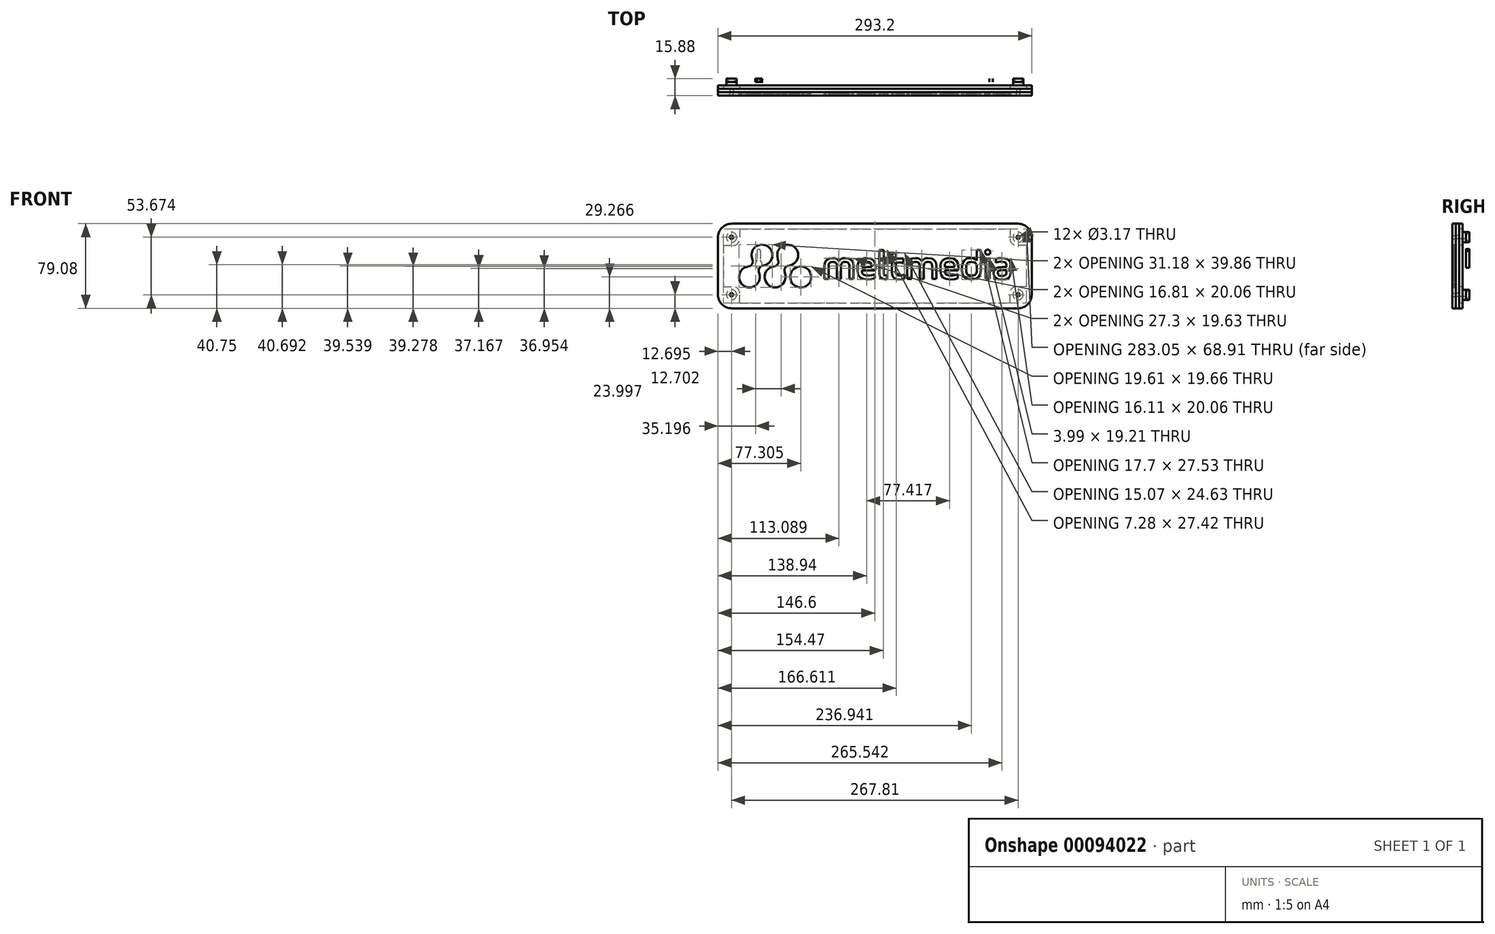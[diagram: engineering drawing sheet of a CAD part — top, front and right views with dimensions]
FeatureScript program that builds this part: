
annotation { "Feature Type Name" : "Feature", "Feature Type Description" : "" }
export const myFeature = defineFeature(function(context is Context, id is Id, definition is map)
    precondition{}
    {
        {
            var Q0;
            Q0=qCreatedBy(makeId("Front.planeOp"),FACE);
            var sketch = newSketch(context, id + "F0", { "sketchPlane" : qUnion([Q0])});
            skLineSegment(sketch, "E0", {"start": v(-43.17, -12.1) * mm, "end": v(-47.16, -12.1) * mm});
            skLineSegment(sketch, "E1", {"start": v(-47.16, -12.1) * mm, "end": v(-47.16, 0.02) * mm});
            skLineSegment(sketch, "E2", {"start": v(-47.16, 0.02) * mm, "end": v(-46.7, 3.2) * mm});
            skLineSegment(sketch, "E3", {"start": v(-46.7, 3.2) * mm, "end": v(-45.25, 5.57) * mm});
            skLineSegment(sketch, "E4", {"start": v(-45.25, 5.57) * mm, "end": v(-42.8, 7.03) * mm});
            skLineSegment(sketch, "E5", {"start": v(-42.8, 7.03) * mm, "end": v(-39.3, 7.53) * mm});
            skLineSegment(sketch, "E6", {"start": v(-39.3, 7.53) * mm, "end": v(-37.27, 7.34) * mm});
            skLineSegment(sketch, "E7", {"start": v(-37.27, 7.34) * mm, "end": v(-35.64, 6.79) * mm});
            skLineSegment(sketch, "E8", {"start": v(-35.64, 6.79) * mm, "end": v(-34.39, 5.9) * mm});
            skLineSegment(sketch, "E9", {"start": v(-34.39, 5.9) * mm, "end": v(-33.5, 4.7) * mm});
            skLineSegment(sketch, "E10", {"start": v(-33.5, 4.7) * mm, "end": v(-32.57, 5.9) * mm});
            skLineSegment(sketch, "E11", {"start": v(-32.57, 5.9) * mm, "end": v(-31.3, 6.79) * mm});
            skLineSegment(sketch, "E12", {"start": v(-31.3, 6.79) * mm, "end": v(-29.67, 7.34) * mm});
            skLineSegment(sketch, "E13", {"start": v(-29.67, 7.34) * mm, "end": v(-27.68, 7.53) * mm});
            skLineSegment(sketch, "E14", {"start": v(-27.68, 7.53) * mm, "end": v(-24.1, 7.04) * mm});
            skLineSegment(sketch, "E15", {"start": v(-24.1, 7.04) * mm, "end": v(-21.68, 5.6) * mm});
            skLineSegment(sketch, "E16", {"start": v(-21.68, 5.6) * mm, "end": v(-20.3, 3.24) * mm});
            skLineSegment(sketch, "E17", {"start": v(-20.3, 3.24) * mm, "end": v(-19.86, 0.02) * mm});
            skLineSegment(sketch, "E18", {"start": v(-19.86, 0.02) * mm, "end": v(-19.86, -12.1) * mm});
            skLineSegment(sketch, "E19", {"start": v(-19.86, -12.1) * mm, "end": v(-23.85, -12.1) * mm});
            skLineSegment(sketch, "E20", {"start": v(-23.85, -12.1) * mm, "end": v(-23.85, 0.02) * mm});
            skLineSegment(sketch, "E21", {"start": v(-23.85, 0.02) * mm, "end": v(-23.88, 0.89) * mm});
            skLineSegment(sketch, "E22", {"start": v(-23.88, 0.89) * mm, "end": v(-24, 1.64) * mm});
            skLineSegment(sketch, "E23", {"start": v(-24, 1.64) * mm, "end": v(-24.23, 2.3) * mm});
            skLineSegment(sketch, "E24", {"start": v(-24.23, 2.3) * mm, "end": v(-24.59, 2.84) * mm});
            skLineSegment(sketch, "E25", {"start": v(-24.59, 2.84) * mm, "end": v(-25.1, 3.26) * mm});
            skLineSegment(sketch, "E26", {"start": v(-25.1, 3.26) * mm, "end": v(-25.76, 3.57) * mm});
            skLineSegment(sketch, "E27", {"start": v(-25.76, 3.57) * mm, "end": v(-26.62, 3.75) * mm});
            skLineSegment(sketch, "E28", {"start": v(-26.62, 3.75) * mm, "end": v(-27.68, 3.82) * mm});
            skLineSegment(sketch, "E29", {"start": v(-27.68, 3.82) * mm, "end": v(-28.76, 3.75) * mm});
            skLineSegment(sketch, "E30", {"start": v(-28.76, 3.75) * mm, "end": v(-29.63, 3.57) * mm});
            skLineSegment(sketch, "E31", {"start": v(-29.63, 3.57) * mm, "end": v(-30.32, 3.26) * mm});
            skLineSegment(sketch, "E32", {"start": v(-30.32, 3.26) * mm, "end": v(-30.83, 2.84) * mm});
            skLineSegment(sketch, "E33", {"start": v(-30.83, 2.84) * mm, "end": v(-31.2, 2.3) * mm});
            skLineSegment(sketch, "E34", {"start": v(-31.2, 2.3) * mm, "end": v(-31.43, 1.64) * mm});
            skLineSegment(sketch, "E35", {"start": v(-31.43, 1.64) * mm, "end": v(-31.56, 0.89) * mm});
            skLineSegment(sketch, "E36", {"start": v(-31.56, 0.89) * mm, "end": v(-31.6, 0.02) * mm});
            skLineSegment(sketch, "E37", {"start": v(-31.6, 0.02) * mm, "end": v(-31.6, -12.1) * mm});
            skLineSegment(sketch, "E38", {"start": v(-31.6, -12.1) * mm, "end": v(-35.47, -12.1) * mm});
            skLineSegment(sketch, "E39", {"start": v(-35.47, -12.1) * mm, "end": v(-35.47, 0.02) * mm});
            skLineSegment(sketch, "E40", {"start": v(-35.47, 0.02) * mm, "end": v(-35.5, 0.89) * mm});
            skLineSegment(sketch, "E41", {"start": v(-35.5, 0.89) * mm, "end": v(-35.62, 1.64) * mm});
            skLineSegment(sketch, "E42", {"start": v(-35.62, 1.64) * mm, "end": v(-35.84, 2.3) * mm});
            skLineSegment(sketch, "E43", {"start": v(-35.84, 2.3) * mm, "end": v(-36.2, 2.84) * mm});
            skLineSegment(sketch, "E44", {"start": v(-36.2, 2.84) * mm, "end": v(-36.7, 3.26) * mm});
            skLineSegment(sketch, "E45", {"start": v(-36.7, 3.26) * mm, "end": v(-37.36, 3.57) * mm});
            skLineSegment(sketch, "E46", {"start": v(-37.36, 3.57) * mm, "end": v(-38.22, 3.75) * mm});
            skLineSegment(sketch, "E47", {"start": v(-38.22, 3.75) * mm, "end": v(-39.3, 3.82) * mm});
            skLineSegment(sketch, "E48", {"start": v(-39.3, 3.82) * mm, "end": v(-40.38, 3.75) * mm});
            skLineSegment(sketch, "E49", {"start": v(-40.38, 3.75) * mm, "end": v(-41.25, 3.57) * mm});
            skLineSegment(sketch, "E50", {"start": v(-41.25, 3.57) * mm, "end": v(-41.92, 3.26) * mm});
            skLineSegment(sketch, "E51", {"start": v(-41.92, 3.26) * mm, "end": v(-42.43, 2.84) * mm});
            skLineSegment(sketch, "E52", {"start": v(-42.43, 2.84) * mm, "end": v(-42.79, 2.3) * mm});
            skLineSegment(sketch, "E53", {"start": v(-42.79, 2.3) * mm, "end": v(-43.01, 1.64) * mm});
            skLineSegment(sketch, "E54", {"start": v(-43.01, 1.64) * mm, "end": v(-43.14, 0.89) * mm});
            skLineSegment(sketch, "E55", {"start": v(-43.14, 0.89) * mm, "end": v(-43.17, 0.02) * mm});
            skLineSegment(sketch, "E56", {"start": v(-43.17, 0.02) * mm, "end": v(-43.17, -12.1) * mm});
            skLineSegment(sketch, "E57", {"start": v(-12.07, -0.71) * mm, "end": v(-3.01, -0.71) * mm});
            skLineSegment(sketch, "E58", {"start": v(-3.01, -0.71) * mm, "end": v(-3.01, 0.25) * mm});
            skLineSegment(sketch, "E59", {"start": v(-3.01, 0.25) * mm, "end": v(-3.32, 1.96) * mm});
            skLineSegment(sketch, "E60", {"start": v(-3.32, 1.96) * mm, "end": v(-4.2, 3.16) * mm});
            skLineSegment(sketch, "E61", {"start": v(-4.2, 3.16) * mm, "end": v(-5.64, 3.86) * mm});
            skLineSegment(sketch, "E62", {"start": v(-5.64, 3.86) * mm, "end": v(-7.58, 4.09) * mm});
            skLineSegment(sketch, "E63", {"start": v(-7.58, 4.09) * mm, "end": v(-9.5, 3.86) * mm});
            skLineSegment(sketch, "E64", {"start": v(-9.5, 3.86) * mm, "end": v(-10.92, 3.16) * mm});
            skLineSegment(sketch, "E65", {"start": v(-10.92, 3.16) * mm, "end": v(-11.78, 1.96) * mm});
            skLineSegment(sketch, "E66", {"start": v(-11.78, 1.96) * mm, "end": v(-12.07, 0.25) * mm});
            skLineSegment(sketch, "E67", {"start": v(-12.07, 0.25) * mm, "end": v(-12.07, -0.71) * mm});
            skLineSegment(sketch, "E68", {"start": v(0.36, -3.97) * mm, "end": v(-12.07, -3.97) * mm});
            skLineSegment(sketch, "E69", {"start": v(-12.07, -3.97) * mm, "end": v(-12.07, -4.82) * mm});
            skLineSegment(sketch, "E70", {"start": v(-12.07, -4.82) * mm, "end": v(-12, -5.8) * mm});
            skLineSegment(sketch, "E71", {"start": v(-12, -5.8) * mm, "end": v(-11.76, -6.63) * mm});
            skLineSegment(sketch, "E72", {"start": v(-11.76, -6.63) * mm, "end": v(-11.35, -7.31) * mm});
            skLineSegment(sketch, "E73", {"start": v(-11.35, -7.31) * mm, "end": v(-10.77, -7.85) * mm});
            skLineSegment(sketch, "E74", {"start": v(-10.77, -7.85) * mm, "end": v(-10, -8.26) * mm});
            skLineSegment(sketch, "E75", {"start": v(-10, -8.26) * mm, "end": v(-9.05, -8.55) * mm});
            skLineSegment(sketch, "E76", {"start": v(-9.05, -8.55) * mm, "end": v(-7.9, -8.72) * mm});
            skLineSegment(sketch, "E77", {"start": v(-7.9, -8.72) * mm, "end": v(-6.54, -8.77) * mm});
            skLineSegment(sketch, "E78", {"start": v(-6.54, -8.77) * mm, "end": v(-4.76, -8.68) * mm});
            skLineSegment(sketch, "E79", {"start": v(-4.76, -8.68) * mm, "end": v(-2.92, -8.44) * mm});
            skLineSegment(sketch, "E80", {"start": v(-2.92, -8.44) * mm, "end": v(-1.24, -8.08) * mm});
            skLineSegment(sketch, "E81", {"start": v(-1.24, -8.08) * mm, "end": v(0.09, -7.65) * mm});
            skLineSegment(sketch, "E82", {"start": v(0.09, -7.65) * mm, "end": v(0.09, -11.4) * mm});
            skLineSegment(sketch, "E83", {"start": v(0.09, -11.4) * mm, "end": v(-3.05, -12.24) * mm});
            skLineSegment(sketch, "E84", {"start": v(-3.05, -12.24) * mm, "end": v(-6.54, -12.53) * mm});
            skLineSegment(sketch, "E85", {"start": v(-6.54, -12.53) * mm, "end": v(-10.74, -12.06) * mm});
            skLineSegment(sketch, "E86", {"start": v(-10.74, -12.06) * mm, "end": v(-13.71, -10.6) * mm});
            skLineSegment(sketch, "E87", {"start": v(-13.71, -10.6) * mm, "end": v(-15.48, -8.03) * mm});
            skLineSegment(sketch, "E88", {"start": v(-15.48, -8.03) * mm, "end": v(-16.06, -4.24) * mm});
            skLineSegment(sketch, "E89", {"start": v(-16.06, -4.24) * mm, "end": v(-16.06, -0.87) * mm});
            skLineSegment(sketch, "E90", {"start": v(-16.06, -0.87) * mm, "end": v(-15.96, 0.88) * mm});
            skLineSegment(sketch, "E91", {"start": v(-15.96, 0.88) * mm, "end": v(-15.63, 2.49) * mm});
            skLineSegment(sketch, "E92", {"start": v(-15.63, 2.49) * mm, "end": v(-15.05, 3.92) * mm});
            skLineSegment(sketch, "E93", {"start": v(-15.05, 3.92) * mm, "end": v(-14.2, 5.15) * mm});
            skLineSegment(sketch, "E94", {"start": v(-14.2, 5.15) * mm, "end": v(-13.03, 6.15) * mm});
            skLineSegment(sketch, "E95", {"start": v(-13.03, 6.15) * mm, "end": v(-11.54, 6.9) * mm});
            skLineSegment(sketch, "E96", {"start": v(-11.54, 6.9) * mm, "end": v(-9.7, 7.37) * mm});
            skLineSegment(sketch, "E97", {"start": v(-9.7, 7.37) * mm, "end": v(-7.46, 7.53) * mm});
            skLineSegment(sketch, "E98", {"start": v(-7.46, 7.53) * mm, "end": v(-3.93, 7.03) * mm});
            skLineSegment(sketch, "E99", {"start": v(-3.93, 7.03) * mm, "end": v(-1.36, 5.52) * mm});
            skLineSegment(sketch, "E100", {"start": v(-1.36, 5.52) * mm, "end": v(0.21, 3.01) * mm});
            skLineSegment(sketch, "E101", {"start": v(0.21, 3.01) * mm, "end": v(0.74, -0.48) * mm});
            skLineSegment(sketch, "E102", {"start": v(0.74, -0.48) * mm, "end": v(0.67, -2.15) * mm});
            skLineSegment(sketch, "E103", {"start": v(0.67, -2.15) * mm, "end": v(0.36, -3.97) * mm});
            skLineSegment(sketch, "E104", {"start": v(4.23, 15) * mm, "end": v(8.22, 15) * mm});
            skLineSegment(sketch, "E105", {"start": v(8.22, 15) * mm, "end": v(8.22, -5.9) * mm});
            skLineSegment(sketch, "E106", {"start": v(8.22, -5.9) * mm, "end": v(8.34, -7.25) * mm});
            skLineSegment(sketch, "E107", {"start": v(8.34, -7.25) * mm, "end": v(8.7, -8.1) * mm});
            skLineSegment(sketch, "E108", {"start": v(8.7, -8.1) * mm, "end": v(9.26, -8.53) * mm});
            skLineSegment(sketch, "E109", {"start": v(9.26, -8.53) * mm, "end": v(10.04, -8.65) * mm});
            skLineSegment(sketch, "E110", {"start": v(10.04, -8.65) * mm, "end": v(10.79, -8.6) * mm});
            skLineSegment(sketch, "E111", {"start": v(10.79, -8.6) * mm, "end": v(11.51, -8.42) * mm});
            skLineSegment(sketch, "E112", {"start": v(11.51, -8.42) * mm, "end": v(11.51, -12.06) * mm});
            skLineSegment(sketch, "E113", {"start": v(11.51, -12.06) * mm, "end": v(10.58, -12.32) * mm});
            skLineSegment(sketch, "E114", {"start": v(10.58, -12.32) * mm, "end": v(9.38, -12.4) * mm});
            skLineSegment(sketch, "E115", {"start": v(9.38, -12.4) * mm, "end": v(7.37, -12.1) * mm});
            skLineSegment(sketch, "E116", {"start": v(7.37, -12.1) * mm, "end": v(5.73, -11.1) * mm});
            skLineSegment(sketch, "E117", {"start": v(5.73, -11.1) * mm, "end": v(4.63, -9.32) * mm});
            skLineSegment(sketch, "E118", {"start": v(4.63, -9.32) * mm, "end": v(4.23, -6.68) * mm});
            skLineSegment(sketch, "E119", {"start": v(4.23, -6.68) * mm, "end": v(4.23, 15) * mm});
            skLineSegment(sketch, "E120", {"start": v(12.48, 6.49) * mm, "end": v(15.85, 7.1) * mm});
            skLineSegment(sketch, "E121", {"start": v(15.85, 7.1) * mm, "end": v(16.5, 12.14) * mm});
            skLineSegment(sketch, "E122", {"start": v(16.5, 12.14) * mm, "end": v(19.8, 12.14) * mm});
            skLineSegment(sketch, "E123", {"start": v(19.8, 12.14) * mm, "end": v(19.8, 7.1) * mm});
            skLineSegment(sketch, "E124", {"start": v(19.8, 7.1) * mm, "end": v(26.85, 7.1) * mm});
            skLineSegment(sketch, "E125", {"start": v(26.85, 7.1) * mm, "end": v(26.85, 3.4) * mm});
            skLineSegment(sketch, "E126", {"start": v(26.85, 3.4) * mm, "end": v(19.8, 3.4) * mm});
            skLineSegment(sketch, "E127", {"start": v(19.8, 3.4) * mm, "end": v(19.8, -5.4) * mm});
            skLineSegment(sketch, "E128", {"start": v(19.8, -5.4) * mm, "end": v(20.01, -7) * mm});
            skLineSegment(sketch, "E129", {"start": v(20.01, -7) * mm, "end": v(20.62, -8.04) * mm});
            skLineSegment(sketch, "E130", {"start": v(20.62, -8.04) * mm, "end": v(21.58, -8.6) * mm});
            skLineSegment(sketch, "E131", {"start": v(21.58, -8.6) * mm, "end": v(22.82, -8.77) * mm});
            skLineSegment(sketch, "E132", {"start": v(22.82, -8.77) * mm, "end": v(24.13, -8.7) * mm});
            skLineSegment(sketch, "E133", {"start": v(24.13, -8.7) * mm, "end": v(25.41, -8.54) * mm});
            skLineSegment(sketch, "E134", {"start": v(25.41, -8.54) * mm, "end": v(26.58, -8.28) * mm});
            skLineSegment(sketch, "E135", {"start": v(26.58, -8.28) * mm, "end": v(27.54, -7.96) * mm});
            skLineSegment(sketch, "E136", {"start": v(27.54, -7.96) * mm, "end": v(27.54, -11.67) * mm});
            skLineSegment(sketch, "E137", {"start": v(27.54, -11.67) * mm, "end": v(25.38, -12.28) * mm});
            skLineSegment(sketch, "E138", {"start": v(25.38, -12.28) * mm, "end": v(22.82, -12.49) * mm});
            skLineSegment(sketch, "E139", {"start": v(22.82, -12.49) * mm, "end": v(20.03, -12.13) * mm});
            skLineSegment(sketch, "E140", {"start": v(20.03, -12.13) * mm, "end": v(17.82, -10.94) * mm});
            skLineSegment(sketch, "E141", {"start": v(17.82, -10.94) * mm, "end": v(16.37, -8.75) * mm});
            skLineSegment(sketch, "E142", {"start": v(16.37, -8.75) * mm, "end": v(15.85, -5.36) * mm});
            skLineSegment(sketch, "E143", {"start": v(15.85, -5.36) * mm, "end": v(15.85, 3.4) * mm});
            skLineSegment(sketch, "E144", {"start": v(15.85, 3.4) * mm, "end": v(12.48, 3.4) * mm});
            skLineSegment(sketch, "E145", {"start": v(12.48, 3.4) * mm, "end": v(12.48, 6.49) * mm});
            skLineSegment(sketch, "E146", {"start": v(34.24, -12.1) * mm, "end": v(30.25, -12.1) * mm});
            skLineSegment(sketch, "E147", {"start": v(30.25, -12.1) * mm, "end": v(30.25, 0.02) * mm});
            skLineSegment(sketch, "E148", {"start": v(30.25, 0.02) * mm, "end": v(30.73, 3.2) * mm});
            skLineSegment(sketch, "E149", {"start": v(30.73, 3.2) * mm, "end": v(32.17, 5.57) * mm});
            skLineSegment(sketch, "E150", {"start": v(32.17, 5.57) * mm, "end": v(34.62, 7.03) * mm});
            skLineSegment(sketch, "E151", {"start": v(34.62, 7.03) * mm, "end": v(38.12, 7.53) * mm});
            skLineSegment(sketch, "E152", {"start": v(38.12, 7.53) * mm, "end": v(40.14, 7.34) * mm});
            skLineSegment(sketch, "E153", {"start": v(40.14, 7.34) * mm, "end": v(41.77, 6.79) * mm});
            skLineSegment(sketch, "E154", {"start": v(41.77, 6.79) * mm, "end": v(43.03, 5.9) * mm});
            skLineSegment(sketch, "E155", {"start": v(43.03, 5.9) * mm, "end": v(43.93, 4.7) * mm});
            skLineSegment(sketch, "E156", {"start": v(43.93, 4.7) * mm, "end": v(44.85, 5.9) * mm});
            skLineSegment(sketch, "E157", {"start": v(44.85, 5.9) * mm, "end": v(46.12, 6.79) * mm});
            skLineSegment(sketch, "E158", {"start": v(46.12, 6.79) * mm, "end": v(47.74, 7.34) * mm});
            skLineSegment(sketch, "E159", {"start": v(47.74, 7.34) * mm, "end": v(49.73, 7.53) * mm});
            skLineSegment(sketch, "E160", {"start": v(49.73, 7.53) * mm, "end": v(53.3, 7.04) * mm});
            skLineSegment(sketch, "E161", {"start": v(53.3, 7.04) * mm, "end": v(55.74, 5.6) * mm});
            skLineSegment(sketch, "E162", {"start": v(55.74, 5.6) * mm, "end": v(57.12, 3.24) * mm});
            skLineSegment(sketch, "E163", {"start": v(57.12, 3.24) * mm, "end": v(57.56, 0.02) * mm});
            skLineSegment(sketch, "E164", {"start": v(57.56, 0.02) * mm, "end": v(57.56, -12.1) * mm});
            skLineSegment(sketch, "E165", {"start": v(57.56, -12.1) * mm, "end": v(53.57, -12.1) * mm});
            skLineSegment(sketch, "E166", {"start": v(53.57, -12.1) * mm, "end": v(53.57, 0.02) * mm});
            skLineSegment(sketch, "E167", {"start": v(53.57, 0.02) * mm, "end": v(53.53, 0.89) * mm});
            skLineSegment(sketch, "E168", {"start": v(53.53, 0.89) * mm, "end": v(53.4, 1.64) * mm});
            skLineSegment(sketch, "E169", {"start": v(53.4, 1.64) * mm, "end": v(53.18, 2.3) * mm});
            skLineSegment(sketch, "E170", {"start": v(53.18, 2.3) * mm, "end": v(52.83, 2.84) * mm});
            skLineSegment(sketch, "E171", {"start": v(52.83, 2.84) * mm, "end": v(52.33, 3.26) * mm});
            skLineSegment(sketch, "E172", {"start": v(52.33, 3.26) * mm, "end": v(51.66, 3.57) * mm});
            skLineSegment(sketch, "E173", {"start": v(51.66, 3.57) * mm, "end": v(50.8, 3.75) * mm});
            skLineSegment(sketch, "E174", {"start": v(50.8, 3.75) * mm, "end": v(49.73, 3.82) * mm});
            skLineSegment(sketch, "E175", {"start": v(49.73, 3.82) * mm, "end": v(48.65, 3.75) * mm});
            skLineSegment(sketch, "E176", {"start": v(48.65, 3.75) * mm, "end": v(47.78, 3.57) * mm});
            skLineSegment(sketch, "E177", {"start": v(47.78, 3.57) * mm, "end": v(47.1, 3.26) * mm});
            skLineSegment(sketch, "E178", {"start": v(47.1, 3.26) * mm, "end": v(46.59, 2.84) * mm});
            skLineSegment(sketch, "E179", {"start": v(46.59, 2.84) * mm, "end": v(46.22, 2.3) * mm});
            skLineSegment(sketch, "E180", {"start": v(46.22, 2.3) * mm, "end": v(45.99, 1.64) * mm});
            skLineSegment(sketch, "E181", {"start": v(45.99, 1.64) * mm, "end": v(45.86, 0.89) * mm});
            skLineSegment(sketch, "E182", {"start": v(45.86, 0.89) * mm, "end": v(45.82, 0.02) * mm});
            skLineSegment(sketch, "E183", {"start": v(45.82, 0.02) * mm, "end": v(45.82, -12.1) * mm});
            skLineSegment(sketch, "E184", {"start": v(45.82, -12.1) * mm, "end": v(41.95, -12.1) * mm});
            skLineSegment(sketch, "E185", {"start": v(41.95, -12.1) * mm, "end": v(41.95, 0.02) * mm});
            skLineSegment(sketch, "E186", {"start": v(41.95, 0.02) * mm, "end": v(41.92, 0.89) * mm});
            skLineSegment(sketch, "E187", {"start": v(41.92, 0.89) * mm, "end": v(41.8, 1.64) * mm});
            skLineSegment(sketch, "E188", {"start": v(41.8, 1.64) * mm, "end": v(41.57, 2.3) * mm});
            skLineSegment(sketch, "E189", {"start": v(41.57, 2.3) * mm, "end": v(41.22, 2.84) * mm});
            skLineSegment(sketch, "E190", {"start": v(41.22, 2.84) * mm, "end": v(40.73, 3.26) * mm});
            skLineSegment(sketch, "E191", {"start": v(40.73, 3.26) * mm, "end": v(40.06, 3.57) * mm});
            skLineSegment(sketch, "E192", {"start": v(40.06, 3.57) * mm, "end": v(39.2, 3.75) * mm});
            skLineSegment(sketch, "E193", {"start": v(39.2, 3.75) * mm, "end": v(38.12, 3.82) * mm});
            skLineSegment(sketch, "E194", {"start": v(38.12, 3.82) * mm, "end": v(37.04, 3.75) * mm});
            skLineSegment(sketch, "E195", {"start": v(37.04, 3.75) * mm, "end": v(36.17, 3.57) * mm});
            skLineSegment(sketch, "E196", {"start": v(36.17, 3.57) * mm, "end": v(35.5, 3.26) * mm});
            skLineSegment(sketch, "E197", {"start": v(35.5, 3.26) * mm, "end": v(34.99, 2.84) * mm});
            skLineSegment(sketch, "E198", {"start": v(34.99, 2.84) * mm, "end": v(34.63, 2.3) * mm});
            skLineSegment(sketch, "E199", {"start": v(34.63, 2.3) * mm, "end": v(34.4, 1.64) * mm});
            skLineSegment(sketch, "E200", {"start": v(34.4, 1.64) * mm, "end": v(34.28, 0.89) * mm});
            skLineSegment(sketch, "E201", {"start": v(34.28, 0.89) * mm, "end": v(34.24, 0.02) * mm});
            skLineSegment(sketch, "E202", {"start": v(34.24, 0.02) * mm, "end": v(34.24, -12.1) * mm});
            skLineSegment(sketch, "E203", {"start": v(65.34, -0.71) * mm, "end": v(74.4, -0.71) * mm});
            skLineSegment(sketch, "E204", {"start": v(74.4, -0.71) * mm, "end": v(74.4, 0.25) * mm});
            skLineSegment(sketch, "E205", {"start": v(74.4, 0.25) * mm, "end": v(74.1, 1.96) * mm});
            skLineSegment(sketch, "E206", {"start": v(74.1, 1.96) * mm, "end": v(73.2, 3.16) * mm});
            skLineSegment(sketch, "E207", {"start": v(73.2, 3.16) * mm, "end": v(71.77, 3.86) * mm});
            skLineSegment(sketch, "E208", {"start": v(71.77, 3.86) * mm, "end": v(69.83, 4.09) * mm});
            skLineSegment(sketch, "E209", {"start": v(69.83, 4.09) * mm, "end": v(67.9, 3.86) * mm});
            skLineSegment(sketch, "E210", {"start": v(67.9, 3.86) * mm, "end": v(66.5, 3.16) * mm});
            skLineSegment(sketch, "E211", {"start": v(66.5, 3.16) * mm, "end": v(65.63, 1.96) * mm});
            skLineSegment(sketch, "E212", {"start": v(65.63, 1.96) * mm, "end": v(65.34, 0.25) * mm});
            skLineSegment(sketch, "E213", {"start": v(65.34, 0.25) * mm, "end": v(65.34, -0.71) * mm});
            skLineSegment(sketch, "E214", {"start": v(77.77, -3.97) * mm, "end": v(65.34, -3.97) * mm});
            skLineSegment(sketch, "E215", {"start": v(65.34, -3.97) * mm, "end": v(65.34, -4.82) * mm});
            skLineSegment(sketch, "E216", {"start": v(65.34, -4.82) * mm, "end": v(65.42, -5.8) * mm});
            skLineSegment(sketch, "E217", {"start": v(65.42, -5.8) * mm, "end": v(65.66, -6.63) * mm});
            skLineSegment(sketch, "E218", {"start": v(65.66, -6.63) * mm, "end": v(66.06, -7.31) * mm});
            skLineSegment(sketch, "E219", {"start": v(66.06, -7.31) * mm, "end": v(66.64, -7.85) * mm});
            skLineSegment(sketch, "E220", {"start": v(66.64, -7.85) * mm, "end": v(67.4, -8.26) * mm});
            skLineSegment(sketch, "E221", {"start": v(67.4, -8.26) * mm, "end": v(68.36, -8.55) * mm});
            skLineSegment(sketch, "E222", {"start": v(68.36, -8.55) * mm, "end": v(69.52, -8.72) * mm});
            skLineSegment(sketch, "E223", {"start": v(69.52, -8.72) * mm, "end": v(70.88, -8.77) * mm});
            skLineSegment(sketch, "E224", {"start": v(70.88, -8.77) * mm, "end": v(72.66, -8.68) * mm});
            skLineSegment(sketch, "E225", {"start": v(72.66, -8.68) * mm, "end": v(74.5, -8.44) * mm});
            skLineSegment(sketch, "E226", {"start": v(74.5, -8.44) * mm, "end": v(76.18, -8.08) * mm});
            skLineSegment(sketch, "E227", {"start": v(76.18, -8.08) * mm, "end": v(77.5, -7.65) * mm});
            skLineSegment(sketch, "E228", {"start": v(77.5, -7.65) * mm, "end": v(77.5, -11.4) * mm});
            skLineSegment(sketch, "E229", {"start": v(77.5, -11.4) * mm, "end": v(74.37, -12.24) * mm});
            skLineSegment(sketch, "E230", {"start": v(74.37, -12.24) * mm, "end": v(70.88, -12.53) * mm});
            skLineSegment(sketch, "E231", {"start": v(70.88, -12.53) * mm, "end": v(66.68, -12.06) * mm});
            skLineSegment(sketch, "E232", {"start": v(66.68, -12.06) * mm, "end": v(63.7, -10.6) * mm});
            skLineSegment(sketch, "E233", {"start": v(63.7, -10.6) * mm, "end": v(61.94, -8.03) * mm});
            skLineSegment(sketch, "E234", {"start": v(61.94, -8.03) * mm, "end": v(61.35, -4.24) * mm});
            skLineSegment(sketch, "E235", {"start": v(61.35, -4.24) * mm, "end": v(61.35, -0.87) * mm});
            skLineSegment(sketch, "E236", {"start": v(61.35, -0.87) * mm, "end": v(61.46, 0.88) * mm});
            skLineSegment(sketch, "E237", {"start": v(61.46, 0.88) * mm, "end": v(61.79, 2.49) * mm});
            skLineSegment(sketch, "E238", {"start": v(61.79, 2.49) * mm, "end": v(62.37, 3.92) * mm});
            skLineSegment(sketch, "E239", {"start": v(62.37, 3.92) * mm, "end": v(63.23, 5.15) * mm});
            skLineSegment(sketch, "E240", {"start": v(63.23, 5.15) * mm, "end": v(64.39, 6.15) * mm});
            skLineSegment(sketch, "E241", {"start": v(64.39, 6.15) * mm, "end": v(65.88, 6.9) * mm});
            skLineSegment(sketch, "E242", {"start": v(65.88, 6.9) * mm, "end": v(67.73, 7.37) * mm});
            skLineSegment(sketch, "E243", {"start": v(67.73, 7.37) * mm, "end": v(69.95, 7.53) * mm});
            skLineSegment(sketch, "E244", {"start": v(69.95, 7.53) * mm, "end": v(73.49, 7.03) * mm});
            skLineSegment(sketch, "E245", {"start": v(73.49, 7.03) * mm, "end": v(76.06, 5.52) * mm});
            skLineSegment(sketch, "E246", {"start": v(76.06, 5.52) * mm, "end": v(77.63, 3.01) * mm});
            skLineSegment(sketch, "E247", {"start": v(77.63, 3.01) * mm, "end": v(78.16, -0.48) * mm});
            skLineSegment(sketch, "E248", {"start": v(78.16, -0.48) * mm, "end": v(78.08, -2.15) * mm});
            skLineSegment(sketch, "E249", {"start": v(78.08, -2.15) * mm, "end": v(77.77, -3.97) * mm});
            skLineSegment(sketch, "E250", {"start": v(85.48, -4.16) * mm, "end": v(85.52, -5.23) * mm});
            skLineSegment(sketch, "E251", {"start": v(85.52, -5.23) * mm, "end": v(85.67, -6.15) * mm});
            skLineSegment(sketch, "E252", {"start": v(85.67, -6.15) * mm, "end": v(85.95, -6.95) * mm});
            skLineSegment(sketch, "E253", {"start": v(85.95, -6.95) * mm, "end": v(86.4, -7.6) * mm});
            skLineSegment(sketch, "E254", {"start": v(86.4, -7.6) * mm, "end": v(87.02, -8.1) * mm});
            skLineSegment(sketch, "E255", {"start": v(87.02, -8.1) * mm, "end": v(87.86, -8.47) * mm});
            skLineSegment(sketch, "E256", {"start": v(87.86, -8.47) * mm, "end": v(88.96, -8.7) * mm});
            skLineSegment(sketch, "E257", {"start": v(88.96, -8.7) * mm, "end": v(90.32, -8.77) * mm});
            skLineSegment(sketch, "E258", {"start": v(90.32, -8.77) * mm, "end": v(91.68, -8.7) * mm});
            skLineSegment(sketch, "E259", {"start": v(91.68, -8.7) * mm, "end": v(92.77, -8.47) * mm});
            skLineSegment(sketch, "E260", {"start": v(92.77, -8.47) * mm, "end": v(93.63, -8.1) * mm});
            skLineSegment(sketch, "E261", {"start": v(93.63, -8.1) * mm, "end": v(94.28, -7.6) * mm});
            skLineSegment(sketch, "E262", {"start": v(94.28, -7.6) * mm, "end": v(94.73, -6.95) * mm});
            skLineSegment(sketch, "E263", {"start": v(94.73, -6.95) * mm, "end": v(95.03, -6.15) * mm});
            skLineSegment(sketch, "E264", {"start": v(95.03, -6.15) * mm, "end": v(95.2, -5.23) * mm});
            skLineSegment(sketch, "E265", {"start": v(95.2, -5.23) * mm, "end": v(95.24, -4.16) * mm});
            skLineSegment(sketch, "E266", {"start": v(95.24, -4.16) * mm, "end": v(95.24, -0.83) * mm});
            skLineSegment(sketch, "E267", {"start": v(95.24, -0.83) * mm, "end": v(95.2, 0.24) * mm});
            skLineSegment(sketch, "E268", {"start": v(95.2, 0.24) * mm, "end": v(95.03, 1.17) * mm});
            skLineSegment(sketch, "E269", {"start": v(95.03, 1.17) * mm, "end": v(94.73, 1.97) * mm});
            skLineSegment(sketch, "E270", {"start": v(94.73, 1.97) * mm, "end": v(94.28, 2.63) * mm});
            skLineSegment(sketch, "E271", {"start": v(94.28, 2.63) * mm, "end": v(93.63, 3.14) * mm});
            skLineSegment(sketch, "E272", {"start": v(93.63, 3.14) * mm, "end": v(92.77, 3.52) * mm});
            skLineSegment(sketch, "E273", {"start": v(92.77, 3.52) * mm, "end": v(91.68, 3.74) * mm});
            skLineSegment(sketch, "E274", {"start": v(91.68, 3.74) * mm, "end": v(90.32, 3.82) * mm});
            skLineSegment(sketch, "E275", {"start": v(90.32, 3.82) * mm, "end": v(88.98, 3.74) * mm});
            skLineSegment(sketch, "E276", {"start": v(88.98, 3.74) * mm, "end": v(87.9, 3.52) * mm});
            skLineSegment(sketch, "E277", {"start": v(87.9, 3.52) * mm, "end": v(87.05, 3.14) * mm});
            skLineSegment(sketch, "E278", {"start": v(87.05, 3.14) * mm, "end": v(86.42, 2.63) * mm});
            skLineSegment(sketch, "E279", {"start": v(86.42, 2.63) * mm, "end": v(85.97, 1.97) * mm});
            skLineSegment(sketch, "E280", {"start": v(85.97, 1.97) * mm, "end": v(85.68, 1.17) * mm});
            skLineSegment(sketch, "E281", {"start": v(85.68, 1.17) * mm, "end": v(85.53, 0.24) * mm});
            skLineSegment(sketch, "E282", {"start": v(85.53, 0.24) * mm, "end": v(85.48, -0.83) * mm});
            skLineSegment(sketch, "E283", {"start": v(85.48, -0.83) * mm, "end": v(85.48, -4.16) * mm});
            skLineSegment(sketch, "E284", {"start": v(99.2, -4.24) * mm, "end": v(98.57, -7.92) * mm});
            skLineSegment(sketch, "E285", {"start": v(98.57, -7.92) * mm, "end": v(96.8, -10.5) * mm});
            skLineSegment(sketch, "E286", {"start": v(96.8, -10.5) * mm, "end": v(94.03, -12.03) * mm});
            skLineSegment(sketch, "E287", {"start": v(94.03, -12.03) * mm, "end": v(90.36, -12.53) * mm});
            skLineSegment(sketch, "E288", {"start": v(90.36, -12.53) * mm, "end": v(86.5, -12.03) * mm});
            skLineSegment(sketch, "E289", {"start": v(86.5, -12.03) * mm, "end": v(83.72, -10.5) * mm});
            skLineSegment(sketch, "E290", {"start": v(83.72, -10.5) * mm, "end": v(82.05, -7.92) * mm});
            skLineSegment(sketch, "E291", {"start": v(82.05, -7.92) * mm, "end": v(81.5, -4.24) * mm});
            skLineSegment(sketch, "E292", {"start": v(81.5, -4.24) * mm, "end": v(81.5, -0.9) * mm});
            skLineSegment(sketch, "E293", {"start": v(81.5, -0.9) * mm, "end": v(81.97, 2.65) * mm});
            skLineSegment(sketch, "E294", {"start": v(81.97, 2.65) * mm, "end": v(83.43, 5.3) * mm});
            skLineSegment(sketch, "E295", {"start": v(83.43, 5.3) * mm, "end": v(85.95, 6.96) * mm});
            skLineSegment(sketch, "E296", {"start": v(85.95, 6.96) * mm, "end": v(89.59, 7.53) * mm});
            skLineSegment(sketch, "E297", {"start": v(89.59, 7.53) * mm, "end": v(91.57, 7.36) * mm});
            skLineSegment(sketch, "E298", {"start": v(91.57, 7.36) * mm, "end": v(93.15, 6.86) * mm});
            skLineSegment(sketch, "E299", {"start": v(93.15, 6.86) * mm, "end": v(94.36, 6.06) * mm});
            skLineSegment(sketch, "E300", {"start": v(94.36, 6.06) * mm, "end": v(95.24, 5.02) * mm});
            skLineSegment(sketch, "E301", {"start": v(95.24, 5.02) * mm, "end": v(95.24, 15) * mm});
            skLineSegment(sketch, "E302", {"start": v(95.24, 15) * mm, "end": v(99.2, 15) * mm});
            skLineSegment(sketch, "E303", {"start": v(99.2, 15) * mm, "end": v(99.2, -4.24) * mm});
            skLineSegment(sketch, "E304", {"start": v(103.49, 7.1) * mm, "end": v(107.48, 7.1) * mm});
            skLineSegment(sketch, "E305", {"start": v(107.48, 7.1) * mm, "end": v(107.48, -12.1) * mm});
            skLineSegment(sketch, "E306", {"start": v(107.48, -12.1) * mm, "end": v(103.49, -12.1) * mm});
            skLineSegment(sketch, "E307", {"start": v(103.49, -12.1) * mm, "end": v(103.49, 7.1) * mm});
            skLineSegment(sketch, "E308", {"start": v(105.5, 15.47) * mm, "end": v(106.46, 15.28) * mm});
            skLineSegment(sketch, "E309", {"start": v(106.46, 15.28) * mm, "end": v(107.23, 14.75) * mm});
            skLineSegment(sketch, "E310", {"start": v(107.23, 14.75) * mm, "end": v(107.75, 13.97) * mm});
            skLineSegment(sketch, "E311", {"start": v(107.75, 13.97) * mm, "end": v(107.94, 13.03) * mm});
            skLineSegment(sketch, "E312", {"start": v(107.94, 13.03) * mm, "end": v(107.75, 12.08) * mm});
            skLineSegment(sketch, "E313", {"start": v(107.75, 12.08) * mm, "end": v(107.23, 11.3) * mm});
            skLineSegment(sketch, "E314", {"start": v(107.23, 11.3) * mm, "end": v(106.46, 10.79) * mm});
            skLineSegment(sketch, "E315", {"start": v(106.46, 10.79) * mm, "end": v(105.5, 10.6) * mm});
            skLineSegment(sketch, "E316", {"start": v(105.5, 10.6) * mm, "end": v(104.54, 10.79) * mm});
            skLineSegment(sketch, "E317", {"start": v(104.54, 10.79) * mm, "end": v(103.76, 11.3) * mm});
            skLineSegment(sketch, "E318", {"start": v(103.76, 11.3) * mm, "end": v(103.22, 12.08) * mm});
            skLineSegment(sketch, "E319", {"start": v(103.22, 12.08) * mm, "end": v(103.02, 13.03) * mm});
            skLineSegment(sketch, "E320", {"start": v(103.02, 13.03) * mm, "end": v(103.22, 13.99) * mm});
            skLineSegment(sketch, "E321", {"start": v(103.22, 13.99) * mm, "end": v(103.76, 14.76) * mm});
            skLineSegment(sketch, "E322", {"start": v(103.76, 14.76) * mm, "end": v(104.54, 15.28) * mm});
            skLineSegment(sketch, "E323", {"start": v(104.54, 15.28) * mm, "end": v(105.5, 15.47) * mm});
            skLineSegment(sketch, "E324", {"start": v(123.05, -3.74) * mm, "end": v(118.79, -3.74) * mm});
            skLineSegment(sketch, "E325", {"start": v(118.79, -3.74) * mm, "end": v(117.06, -3.89) * mm});
            skLineSegment(sketch, "E326", {"start": v(117.06, -3.89) * mm, "end": v(115.84, -4.37) * mm});
            skLineSegment(sketch, "E327", {"start": v(115.84, -4.37) * mm, "end": v(115.11, -5.22) * mm});
            skLineSegment(sketch, "E328", {"start": v(115.11, -5.22) * mm, "end": v(114.88, -6.49) * mm});
            skLineSegment(sketch, "E329", {"start": v(114.88, -6.49) * mm, "end": v(115.19, -7.87) * mm});
            skLineSegment(sketch, "E330", {"start": v(115.19, -7.87) * mm, "end": v(116.03, -8.68) * mm});
            skLineSegment(sketch, "E331", {"start": v(116.03, -8.68) * mm, "end": v(117.24, -9.06) * mm});
            skLineSegment(sketch, "E332", {"start": v(117.24, -9.06) * mm, "end": v(118.67, -9.16) * mm});
            skLineSegment(sketch, "E333", {"start": v(118.67, -9.16) * mm, "end": v(119.58, -9.14) * mm});
            skLineSegment(sketch, "E334", {"start": v(119.58, -9.14) * mm, "end": v(120.41, -9.06) * mm});
            skLineSegment(sketch, "E335", {"start": v(120.41, -9.06) * mm, "end": v(121.16, -8.9) * mm});
            skLineSegment(sketch, "E336", {"start": v(121.16, -8.9) * mm, "end": v(121.8, -8.63) * mm});
            skLineSegment(sketch, "E337", {"start": v(121.8, -8.63) * mm, "end": v(122.32, -8.25) * mm});
            skLineSegment(sketch, "E338", {"start": v(122.32, -8.25) * mm, "end": v(122.72, -7.72) * mm});
            skLineSegment(sketch, "E339", {"start": v(122.72, -7.72) * mm, "end": v(122.96, -7.02) * mm});
            skLineSegment(sketch, "E340", {"start": v(122.96, -7.02) * mm, "end": v(123.05, -6.14) * mm});
            skLineSegment(sketch, "E341", {"start": v(123.05, -6.14) * mm, "end": v(123.05, -3.74) * mm});
            skLineSegment(sketch, "E342", {"start": v(127, -6.33) * mm, "end": v(126.51, -9.1) * mm});
            skLineSegment(sketch, "E343", {"start": v(126.51, -9.1) * mm, "end": v(125.02, -11.03) * mm});
            skLineSegment(sketch, "E344", {"start": v(125.02, -11.03) * mm, "end": v(122.45, -12.16) * mm});
            skLineSegment(sketch, "E345", {"start": v(122.45, -12.16) * mm, "end": v(118.75, -12.53) * mm});
            skLineSegment(sketch, "E346", {"start": v(118.75, -12.53) * mm, "end": v(115.4, -12.17) * mm});
            skLineSegment(sketch, "E347", {"start": v(115.4, -12.17) * mm, "end": v(112.93, -11.08) * mm});
            skLineSegment(sketch, "E348", {"start": v(112.93, -11.08) * mm, "end": v(111.4, -9.23) * mm});
            skLineSegment(sketch, "E349", {"start": v(111.4, -9.23) * mm, "end": v(110.89, -6.56) * mm});
            skLineSegment(sketch, "E350", {"start": v(110.89, -6.56) * mm, "end": v(111.44, -3.82) * mm});
            skLineSegment(sketch, "E351", {"start": v(111.44, -3.82) * mm, "end": v(113.02, -2.01) * mm});
            skLineSegment(sketch, "E352", {"start": v(113.02, -2.01) * mm, "end": v(115.51, -1.02) * mm});
            skLineSegment(sketch, "E353", {"start": v(115.51, -1.02) * mm, "end": v(118.79, -0.71) * mm});
            skLineSegment(sketch, "E354", {"start": v(118.79, -0.71) * mm, "end": v(123.05, -0.71) * mm});
            skLineSegment(sketch, "E355", {"start": v(123.05, -0.71) * mm, "end": v(123.05, 1.18) * mm});
            skLineSegment(sketch, "E356", {"start": v(123.05, 1.18) * mm, "end": v(122.72, 2.66) * mm});
            skLineSegment(sketch, "E357", {"start": v(122.72, 2.66) * mm, "end": v(121.8, 3.56) * mm});
            skLineSegment(sketch, "E358", {"start": v(121.8, 3.56) * mm, "end": v(120.35, 4) * mm});
            skLineSegment(sketch, "E359", {"start": v(120.35, 4) * mm, "end": v(118.48, 4.13) * mm});
            skLineSegment(sketch, "E360", {"start": v(118.48, 4.13) * mm, "end": v(116.83, 4.08) * mm});
            skLineSegment(sketch, "E361", {"start": v(116.83, 4.08) * mm, "end": v(115.33, 3.93) * mm});
            skLineSegment(sketch, "E362", {"start": v(115.33, 3.93) * mm, "end": v(114.04, 3.7) * mm});
            skLineSegment(sketch, "E363", {"start": v(114.04, 3.7) * mm, "end": v(112.98, 3.4) * mm});
            skLineSegment(sketch, "E364", {"start": v(112.98, 3.4) * mm, "end": v(112.98, 6.88) * mm});
            skLineSegment(sketch, "E365", {"start": v(112.98, 6.88) * mm, "end": v(115.35, 7.38) * mm});
            skLineSegment(sketch, "E366", {"start": v(115.35, 7.38) * mm, "end": v(118.24, 7.53) * mm});
            skLineSegment(sketch, "E367", {"start": v(118.24, 7.53) * mm, "end": v(121.82, 7.22) * mm});
            skLineSegment(sketch, "E368", {"start": v(121.82, 7.22) * mm, "end": v(124.58, 6.17) * mm});
            skLineSegment(sketch, "E369", {"start": v(124.58, 6.17) * mm, "end": v(126.36, 4.22) * mm});
            skLineSegment(sketch, "E370", {"start": v(126.36, 4.22) * mm, "end": v(127, 1.18) * mm});
            skLineSegment(sketch, "E371", {"start": v(127, 1.18) * mm, "end": v(127, -6.33) * mm});
            skLineSegment(sketch, "E372", {"start": v(-108.54, -3.51) * mm, "end": v(-108.37, -5.42) * mm});
            skLineSegment(sketch, "E373", {"start": v(-108.37, -5.42) * mm, "end": v(-107.9, -7.14) * mm});
            skLineSegment(sketch, "E374", {"start": v(-107.9, -7.14) * mm, "end": v(-107.5, -8.89) * mm});
            skLineSegment(sketch, "E375", {"start": v(-107.5, -8.89) * mm, "end": v(-107.43, -10.95) * mm});
            skLineSegment(sketch, "E376", {"start": v(-107.43, -10.95) * mm, "end": v(-108.25, -14.2) * mm});
            skLineSegment(sketch, "E377", {"start": v(-108.25, -14.2) * mm, "end": v(-110, -16.86) * mm});
            skLineSegment(sketch, "E378", {"start": v(-110, -16.86) * mm, "end": v(-112.5, -18.78) * mm});
            skLineSegment(sketch, "E379", {"start": v(-112.5, -18.78) * mm, "end": v(-115.5, -19.84) * mm});
            skLineSegment(sketch, "E380", {"start": v(-115.5, -19.84) * mm, "end": v(-119.2, -19.84) * mm});
            skLineSegment(sketch, "E381", {"start": v(-119.2, -19.84) * mm, "end": v(-122.3, -18.63) * mm});
            skLineSegment(sketch, "E382", {"start": v(-122.3, -18.63) * mm, "end": v(-124.7, -16.56) * mm});
            skLineSegment(sketch, "E383", {"start": v(-124.7, -16.56) * mm, "end": v(-126.27, -13.99) * mm});
            skLineSegment(sketch, "E384", {"start": v(-126.27, -13.99) * mm, "end": v(-127, -10.53) * mm});
            skLineSegment(sketch, "E385", {"start": v(-127, -10.53) * mm, "end": v(-126.45, -6.85) * mm});
            skLineSegment(sketch, "E386", {"start": v(-126.45, -6.85) * mm, "end": v(-125.4, -4.76) * mm});
            skLineSegment(sketch, "E387", {"start": v(-125.4, -4.76) * mm, "end": v(-123.94, -3) * mm});
            skLineSegment(sketch, "E388", {"start": v(-123.94, -3) * mm, "end": v(-122.07, -1.62) * mm});
            skLineSegment(sketch, "E389", {"start": v(-122.07, -1.62) * mm, "end": v(-119.83, -0.7) * mm});
            skLineSegment(sketch, "E390", {"start": v(-119.83, -0.7) * mm, "end": v(-118.16, -0.3) * mm});
            skLineSegment(sketch, "E391", {"start": v(-118.16, -0.3) * mm, "end": v(-116.56, 0.24) * mm});
            skLineSegment(sketch, "E392", {"start": v(-116.56, 0.24) * mm, "end": v(-115.59, 0.85) * mm});
            skLineSegment(sketch, "E393", {"start": v(-115.59, 0.85) * mm, "end": v(-114.78, 1.74) * mm});
            skLineSegment(sketch, "E394", {"start": v(-114.78, 1.74) * mm, "end": v(-114.23, 2.87) * mm});
            skLineSegment(sketch, "E395", {"start": v(-114.23, 2.87) * mm, "end": v(-114.04, 4.21) * mm});
            skLineSegment(sketch, "E396", {"start": v(-114.04, 4.21) * mm, "end": v(-114.27, 5.57) * mm});
            skLineSegment(sketch, "E397", {"start": v(-114.27, 5.57) * mm, "end": v(-114.68, 6.85) * mm});
            skLineSegment(sketch, "E398", {"start": v(-114.68, 6.85) * mm, "end": v(-115.2, 9.6) * mm});
            skLineSegment(sketch, "E399", {"start": v(-115.2, 9.6) * mm, "end": v(-115.21, 11.06) * mm});
            skLineSegment(sketch, "E400", {"start": v(-115.21, 11.06) * mm, "end": v(-115, 12.45) * mm});
            skLineSegment(sketch, "E401", {"start": v(-115, 12.45) * mm, "end": v(-114.63, 13.75) * mm});
            skLineSegment(sketch, "E402", {"start": v(-114.63, 13.75) * mm, "end": v(-114.1, 14.92) * mm});
            skLineSegment(sketch, "E403", {"start": v(-114.1, 14.92) * mm, "end": v(-112.8, 16.78) * mm});
            skLineSegment(sketch, "E404", {"start": v(-112.8, 16.78) * mm, "end": v(-111, 18.38) * mm});
            skLineSegment(sketch, "E405", {"start": v(-111, 18.38) * mm, "end": v(-108.75, 19.48) * mm});
            skLineSegment(sketch, "E406", {"start": v(-108.75, 19.48) * mm, "end": v(-105.96, 20.02) * mm});
            skLineSegment(sketch, "E407", {"start": v(-105.96, 20.02) * mm, "end": v(-103.98, 19.94) * mm});
            skLineSegment(sketch, "E408", {"start": v(-103.98, 19.94) * mm, "end": v(-102.14, 19.47) * mm});
            skLineSegment(sketch, "E409", {"start": v(-102.14, 19.47) * mm, "end": v(-100.51, 18.72) * mm});
            skLineSegment(sketch, "E410", {"start": v(-100.51, 18.72) * mm, "end": v(-99.17, 17.8) * mm});
            skLineSegment(sketch, "E411", {"start": v(-99.17, 17.8) * mm, "end": v(-98.04, 16.7) * mm});
            skLineSegment(sketch, "E412", {"start": v(-98.04, 16.7) * mm, "end": v(-97.09, 15.43) * mm});
            skLineSegment(sketch, "E413", {"start": v(-97.09, 15.43) * mm, "end": v(-96.34, 13.94) * mm});
            skLineSegment(sketch, "E414", {"start": v(-96.34, 13.94) * mm, "end": v(-95.84, 12.17) * mm});
            skLineSegment(sketch, "E415", {"start": v(-95.84, 12.17) * mm, "end": v(-95.81, 8.28) * mm});
            skLineSegment(sketch, "E416", {"start": v(-95.81, 8.28) * mm, "end": v(-97.1, 5.02) * mm});
            skLineSegment(sketch, "E417", {"start": v(-97.1, 5.02) * mm, "end": v(-99.32, 2.54) * mm});
            skLineSegment(sketch, "E418", {"start": v(-99.32, 2.54) * mm, "end": v(-102.1, 1) * mm});
            skLineSegment(sketch, "E419", {"start": v(-102.1, 1) * mm, "end": v(-104.1, 0.52) * mm});
            skLineSegment(sketch, "E420", {"start": v(-104.1, 0.52) * mm, "end": v(-106.08, -0.06) * mm});
            skLineSegment(sketch, "E421", {"start": v(-106.08, -0.06) * mm, "end": v(-106.94, -0.59) * mm});
            skLineSegment(sketch, "E422", {"start": v(-106.94, -0.59) * mm, "end": v(-107.69, -1.34) * mm});
            skLineSegment(sketch, "E423", {"start": v(-107.69, -1.34) * mm, "end": v(-108.25, -2.31) * mm});
            skLineSegment(sketch, "E424", {"start": v(-108.25, -2.31) * mm, "end": v(-108.54, -3.51) * mm});
            skLineSegment(sketch, "E425", {"start": v(-84.54, -3.51) * mm, "end": v(-84.37, -5.42) * mm});
            skLineSegment(sketch, "E426", {"start": v(-84.37, -5.42) * mm, "end": v(-83.9, -7.14) * mm});
            skLineSegment(sketch, "E427", {"start": v(-83.9, -7.14) * mm, "end": v(-83.5, -8.89) * mm});
            skLineSegment(sketch, "E428", {"start": v(-83.5, -8.89) * mm, "end": v(-83.43, -10.95) * mm});
            skLineSegment(sketch, "E429", {"start": v(-83.43, -10.95) * mm, "end": v(-84.25, -14.2) * mm});
            skLineSegment(sketch, "E430", {"start": v(-84.25, -14.2) * mm, "end": v(-86, -16.86) * mm});
            skLineSegment(sketch, "E431", {"start": v(-86, -16.86) * mm, "end": v(-88.5, -18.78) * mm});
            skLineSegment(sketch, "E432", {"start": v(-88.5, -18.78) * mm, "end": v(-91.5, -19.84) * mm});
            skLineSegment(sketch, "E433", {"start": v(-91.5, -19.84) * mm, "end": v(-95.2, -19.84) * mm});
            skLineSegment(sketch, "E434", {"start": v(-95.2, -19.84) * mm, "end": v(-98.3, -18.63) * mm});
            skLineSegment(sketch, "E435", {"start": v(-98.3, -18.63) * mm, "end": v(-100.7, -16.56) * mm});
            skLineSegment(sketch, "E436", {"start": v(-100.7, -16.56) * mm, "end": v(-102.28, -13.99) * mm});
            skLineSegment(sketch, "E437", {"start": v(-102.28, -13.99) * mm, "end": v(-103, -10.53) * mm});
            skLineSegment(sketch, "E438", {"start": v(-103, -10.53) * mm, "end": v(-102.45, -6.85) * mm});
            skLineSegment(sketch, "E439", {"start": v(-102.45, -6.85) * mm, "end": v(-101.4, -4.76) * mm});
            skLineSegment(sketch, "E440", {"start": v(-101.4, -4.76) * mm, "end": v(-99.94, -3) * mm});
            skLineSegment(sketch, "E441", {"start": v(-99.94, -3) * mm, "end": v(-98.08, -1.62) * mm});
            skLineSegment(sketch, "E442", {"start": v(-98.08, -1.62) * mm, "end": v(-95.84, -0.7) * mm});
            skLineSegment(sketch, "E443", {"start": v(-95.84, -0.7) * mm, "end": v(-94.16, -0.3) * mm});
            skLineSegment(sketch, "E444", {"start": v(-94.16, -0.3) * mm, "end": v(-92.56, 0.24) * mm});
            skLineSegment(sketch, "E445", {"start": v(-92.56, 0.24) * mm, "end": v(-91.59, 0.85) * mm});
            skLineSegment(sketch, "E446", {"start": v(-91.59, 0.85) * mm, "end": v(-90.78, 1.74) * mm});
            skLineSegment(sketch, "E447", {"start": v(-90.78, 1.74) * mm, "end": v(-90.24, 2.87) * mm});
            skLineSegment(sketch, "E448", {"start": v(-90.24, 2.87) * mm, "end": v(-90.04, 4.21) * mm});
            skLineSegment(sketch, "E449", {"start": v(-90.04, 4.21) * mm, "end": v(-90.28, 5.57) * mm});
            skLineSegment(sketch, "E450", {"start": v(-90.28, 5.57) * mm, "end": v(-90.69, 6.85) * mm});
            skLineSegment(sketch, "E451", {"start": v(-90.69, 6.85) * mm, "end": v(-91.21, 9.6) * mm});
            skLineSegment(sketch, "E452", {"start": v(-91.21, 9.6) * mm, "end": v(-91.22, 11.06) * mm});
            skLineSegment(sketch, "E453", {"start": v(-91.22, 11.06) * mm, "end": v(-91.01, 12.45) * mm});
            skLineSegment(sketch, "E454", {"start": v(-91.01, 12.45) * mm, "end": v(-90.63, 13.75) * mm});
            skLineSegment(sketch, "E455", {"start": v(-90.63, 13.75) * mm, "end": v(-90.1, 14.92) * mm});
            skLineSegment(sketch, "E456", {"start": v(-90.1, 14.92) * mm, "end": v(-88.8, 16.78) * mm});
            skLineSegment(sketch, "E457", {"start": v(-88.8, 16.78) * mm, "end": v(-87, 18.38) * mm});
            skLineSegment(sketch, "E458", {"start": v(-87, 18.38) * mm, "end": v(-84.76, 19.48) * mm});
            skLineSegment(sketch, "E459", {"start": v(-84.76, 19.48) * mm, "end": v(-81.96, 20.02) * mm});
            skLineSegment(sketch, "E460", {"start": v(-81.96, 20.02) * mm, "end": v(-79.99, 19.94) * mm});
            skLineSegment(sketch, "E461", {"start": v(-79.99, 19.94) * mm, "end": v(-78.14, 19.47) * mm});
            skLineSegment(sketch, "E462", {"start": v(-78.14, 19.47) * mm, "end": v(-76.52, 18.72) * mm});
            skLineSegment(sketch, "E463", {"start": v(-76.52, 18.72) * mm, "end": v(-75.18, 17.8) * mm});
            skLineSegment(sketch, "E464", {"start": v(-75.18, 17.8) * mm, "end": v(-74.05, 16.7) * mm});
            skLineSegment(sketch, "E465", {"start": v(-74.05, 16.7) * mm, "end": v(-73.1, 15.43) * mm});
            skLineSegment(sketch, "E466", {"start": v(-73.1, 15.43) * mm, "end": v(-72.34, 13.94) * mm});
            skLineSegment(sketch, "E467", {"start": v(-72.34, 13.94) * mm, "end": v(-71.84, 12.17) * mm});
            skLineSegment(sketch, "E468", {"start": v(-71.84, 12.17) * mm, "end": v(-71.82, 8.28) * mm});
            skLineSegment(sketch, "E469", {"start": v(-71.82, 8.28) * mm, "end": v(-73.1, 5.02) * mm});
            skLineSegment(sketch, "E470", {"start": v(-73.1, 5.02) * mm, "end": v(-75.32, 2.54) * mm});
            skLineSegment(sketch, "E471", {"start": v(-75.32, 2.54) * mm, "end": v(-78.1, 1) * mm});
            skLineSegment(sketch, "E472", {"start": v(-78.1, 1) * mm, "end": v(-80.1, 0.52) * mm});
            skLineSegment(sketch, "E473", {"start": v(-80.1, 0.52) * mm, "end": v(-82.08, -0.06) * mm});
            skLineSegment(sketch, "E474", {"start": v(-82.08, -0.06) * mm, "end": v(-82.94, -0.59) * mm});
            skLineSegment(sketch, "E475", {"start": v(-82.94, -0.59) * mm, "end": v(-83.69, -1.34) * mm});
            skLineSegment(sketch, "E476", {"start": v(-83.69, -1.34) * mm, "end": v(-84.25, -2.31) * mm});
            skLineSegment(sketch, "E477", {"start": v(-84.25, -2.31) * mm, "end": v(-84.54, -3.51) * mm});
            skLineSegment(sketch, "E478", {"start": v(-72.78, -19.37) * mm, "end": v(-75.06, -18.13) * mm});
            skLineSegment(sketch, "E479", {"start": v(-75.06, -18.13) * mm, "end": v(-77.01, -16.28) * mm});
            skLineSegment(sketch, "E480", {"start": v(-77.01, -16.28) * mm, "end": v(-78.43, -13.85) * mm});
            skLineSegment(sketch, "E481", {"start": v(-78.43, -13.85) * mm, "end": v(-79.1, -10.88) * mm});
            skLineSegment(sketch, "E482", {"start": v(-79.1, -10.88) * mm, "end": v(-79, -8.63) * mm});
            skLineSegment(sketch, "E483", {"start": v(-79, -8.63) * mm, "end": v(-78.48, -6.67) * mm});
            skLineSegment(sketch, "E484", {"start": v(-78.48, -6.67) * mm, "end": v(-77.66, -5) * mm});
            skLineSegment(sketch, "E485", {"start": v(-77.66, -5) * mm, "end": v(-76.64, -3.63) * mm});
            skLineSegment(sketch, "E486", {"start": v(-76.64, -3.63) * mm, "end": v(-75.44, -2.46) * mm});
            skLineSegment(sketch, "E487", {"start": v(-75.44, -2.46) * mm, "end": v(-73.95, -1.46) * mm});
            skLineSegment(sketch, "E488", {"start": v(-73.95, -1.46) * mm, "end": v(-72.18, -0.74) * mm});
            skLineSegment(sketch, "E489", {"start": v(-72.18, -0.74) * mm, "end": v(-70.08, -0.35) * mm});
            skLineSegment(sketch, "E490", {"start": v(-70.08, -0.35) * mm, "end": v(-66.82, -0.6) * mm});
            skLineSegment(sketch, "E491", {"start": v(-66.82, -0.6) * mm, "end": v(-64.1, -1.73) * mm});
            skLineSegment(sketch, "E492", {"start": v(-64.1, -1.73) * mm, "end": v(-61.96, -3.47) * mm});
            skLineSegment(sketch, "E493", {"start": v(-61.96, -3.47) * mm, "end": v(-60.49, -5.56) * mm});
            skLineSegment(sketch, "E494", {"start": v(-60.49, -5.56) * mm, "end": v(-59.5, -8.52) * mm});
            skLineSegment(sketch, "E495", {"start": v(-59.5, -8.52) * mm, "end": v(-59.5, -11.77) * mm});
            skLineSegment(sketch, "E496", {"start": v(-59.5, -11.77) * mm, "end": v(-60.06, -13.78) * mm});
            skLineSegment(sketch, "E497", {"start": v(-60.06, -13.78) * mm, "end": v(-61.06, -15.63) * mm});
            skLineSegment(sketch, "E498", {"start": v(-61.06, -15.63) * mm, "end": v(-62.42, -17.26) * mm});
            skLineSegment(sketch, "E499", {"start": v(-62.42, -17.26) * mm, "end": v(-64.1, -18.58) * mm});
            skLineSegment(sketch, "E500", {"start": v(-64.1, -18.58) * mm, "end": v(-66.03, -19.52) * mm});
            skLineSegment(sketch, "E501", {"start": v(-66.03, -19.52) * mm, "end": v(-68.15, -20.02) * mm});
            skLineSegment(sketch, "E502", {"start": v(-68.15, -20.02) * mm, "end": v(-70.42, -20) * mm});
            skLineSegment(sketch, "E503", {"start": v(-70.42, -20) * mm, "end": v(-72.78, -19.37) * mm});
            skLineSegment(sketch, "E504.bottom", {"start": v(-133.9, 39.63) * mm, "end": v(133.9, 39.63) * mm});
            skLineSegment(sketch, "E504.top", {"start": v(-133.9, -39.45) * mm, "end": v(133.9, -39.45) * mm});
            skLineSegment(sketch, "E504.left", {"start": v(-146.6, 26.93) * mm, "end": v(-146.6, -26.75) * mm});
            skLineSegment(sketch, "E504.right", {"start": v(146.6, 26.93) * mm, "end": v(146.6, -26.75) * mm});
            skPoint(sketch, "E505.visualSharp", {"position": v(-146.6, 39.63) * mm});
            skArc(sketch, "E505.filletArc", {"start": v(-133.9, 39.63) * mm, "mid": v(-142.89, 35.9) * mm, "end": v(-146.6, 26.93) * mm});
            skPoint(sketch, "E506.visualSharp", {"position": v(146.6, 39.63) * mm});
            skArc(sketch, "E506.filletArc", {"start": v(146.6, 26.93) * mm, "mid": v(142.89, 35.9) * mm, "end": v(133.9, 39.63) * mm});
            skPoint(sketch, "E507.visualSharp", {"position": v(146.6, -39.45) * mm});
            skArc(sketch, "E507.filletArc", {"start": v(133.9, -39.45) * mm, "mid": v(142.89, -35.73) * mm, "end": v(146.6, -26.75) * mm});
            skPoint(sketch, "E508.visualSharp", {"position": v(-146.6, -39.45) * mm});
            skArc(sketch, "E508.filletArc", {"start": v(-146.6, -26.75) * mm, "mid": v(-142.89, -35.73) * mm, "end": v(-133.9, -39.45) * mm});
            skCircle(sketch, "E509", {"center": v(-133.9, 26.93) * mm, "radius": 1.59 * mm});
            skCircle(sketch, "E510", {"center": v(-133.9, -26.75) * mm, "radius": 1.59 * mm});
            skCircle(sketch, "E511", {"center": v(133.9, 26.93) * mm, "radius": 1.59 * mm});
            skCircle(sketch, "E512", {"center": v(133.9, -26.75) * mm, "radius": 1.59 * mm});
            skSolve(sketch);
        }
        {
            var Q0;
            Q0=makeQuery(id+"F0.imprint","IMPRINT",FACE,{"disambiguationData":[TD([[makeQuery(id+"F0.imprint","IMPRINT",EDGE,{"derivedFrom":sQuery(id+"F0.wireOp",EDGE,"E0")}),1.0]])]});
            var Q1;
            Q1=makeQuery(id+"F0.imprint","IMPRINT",FACE,{"disambiguationData":[TD([[makeQuery(id+"F0.imprint","IMPRINT",EDGE,{"derivedFrom":sQuery(id+"F0.wireOp",EDGE,"E57")}),1.0]])]});
            var Q2;
            Q2=makeQuery(id+"F0.imprint","IMPRINT",FACE,{"disambiguationData":[TD([[makeQuery(id+"F0.imprint","IMPRINT",EDGE,{"derivedFrom":sQuery(id+"F0.wireOp",EDGE,"E203")}),1.0]])]});
            var Q3;
            Q3=makeQuery(id+"F0.imprint","IMPRINT",FACE,{"disambiguationData":[TD([[makeQuery(id+"F0.imprint","IMPRINT",EDGE,{"derivedFrom":sQuery(id+"F0.wireOp",EDGE,"E250")}),1.0]])]});
            var Q4;
            Q4=makeQuery(id+"F0.imprint","IMPRINT",FACE,{"disambiguationData":[TD([[makeQuery(id+"F0.imprint","IMPRINT",EDGE,{"derivedFrom":sQuery(id+"F0.wireOp",EDGE,"E324")}),1.0]])]});
            extrude(context, id + "F1", {"entities" : qUnion([Q0, Q1, Q2, Q3, Q4]), "depth" : 3.17 * mm});
        }
        {
            var Q0;
            Q0=makeQuery(id+"F0.imprint","IMPRINT",FACE,{"disambiguationData":[TD([[makeQuery(id+"F0.imprint","IMPRINT",EDGE,{"derivedFrom":sQuery(id+"F0.wireOp",EDGE,"E57")}),1.0]])]});
            var Q1;
            Q1=makeQuery(id+"F0.imprint","IMPRINT",FACE,{"disambiguationData":[TD([[makeQuery(id+"F0.imprint","IMPRINT",EDGE,{"derivedFrom":sQuery(id+"F0.wireOp",EDGE,"E0")}),-1.0]])]});
            var Q2;
            Q2=makeQuery(id+"F0.imprint","IMPRINT",FACE,{"disambiguationData":[TD([[makeQuery(id+"F0.imprint","IMPRINT",EDGE,{"derivedFrom":sQuery(id+"F0.wireOp",EDGE,"E0")}),1.0]])]});
            var Q3;
            Q3=makeQuery(id+"F0.imprint","IMPRINT",FACE,{"disambiguationData":[TD([[makeQuery(id+"F0.imprint","IMPRINT",EDGE,{"derivedFrom":sQuery(id+"F0.wireOp",EDGE,"E324")}),-1.0]])]});
            var Q4;
            Q4=makeQuery(id+"F0.imprint","IMPRINT",FACE,{"disambiguationData":[TD([[makeQuery(id+"F0.imprint","IMPRINT",EDGE,{"derivedFrom":sQuery(id+"F0.wireOp",EDGE,"E250")}),-1.0]])]});
            var Q5;
            Q5=makeQuery(id+"F0.imprint","IMPRINT",FACE,{"disambiguationData":[TD([[makeQuery(id+"F0.imprint","IMPRINT",EDGE,{"derivedFrom":sQuery(id+"F0.wireOp",EDGE,"E120")}),-1.0]])]});
            var Q6;
            Q6=makeQuery(id+"F0.imprint","IMPRINT",FACE,{"disambiguationData":[TD([[makeQuery(id+"F0.imprint","IMPRINT",EDGE,{"derivedFrom":sQuery(id+"F0.wireOp",EDGE,"E203")}),-1.0]])]});
            var Q7;
            Q7=makeQuery(id+"F0.imprint","IMPRINT",FACE,{"disambiguationData":[TD([[makeQuery(id+"F0.imprint","IMPRINT",EDGE,{"derivedFrom":sQuery(id+"F0.wireOp",EDGE,"E57")}),-1.0]])]});
            var Q8;
            Q8=makeQuery(id+"F0.imprint","IMPRINT",FACE,{"disambiguationData":[TD([[makeQuery(id+"F0.imprint","IMPRINT",EDGE,{"derivedFrom":sQuery(id+"F0.wireOp",EDGE,"E146")}),-1.0]])]});
            var Q9;
            Q9=makeQuery(id+"F0.imprint","IMPRINT",FACE,{"disambiguationData":[TD([[makeQuery(id+"F0.imprint","IMPRINT",EDGE,{"derivedFrom":sQuery(id+"F0.wireOp",EDGE,"E104")}),-1.0]])]});
            var Q10;
            Q10=makeQuery(id+"F0.imprint","IMPRINT",FACE,{"disambiguationData":[TD([[makeQuery(id+"F0.imprint","IMPRINT",EDGE,{"derivedFrom":sQuery(id+"F0.wireOp",EDGE,"E203")}),1.0]])]});
            var Q11;
            Q11=makeQuery(id+"F0.imprint","IMPRINT",FACE,{"disambiguationData":[TD([[makeQuery(id+"F0.imprint","IMPRINT",EDGE,{"derivedFrom":sQuery(id+"F0.wireOp",EDGE,"E250")}),1.0]])]});
            var Q12;
            Q12=makeQuery(id+"F0.imprint","IMPRINT",FACE,{"disambiguationData":[TD([[makeQuery(id+"F0.imprint","IMPRINT",EDGE,{"derivedFrom":sQuery(id+"F0.wireOp",EDGE,"E304")}),-1.0]])]});
            var Q13;
            Q13=makeQuery(id+"F0.imprint","IMPRINT",FACE,{"disambiguationData":[TD([[makeQuery(id+"F0.imprint","IMPRINT",EDGE,{"derivedFrom":sQuery(id+"F0.wireOp",EDGE,"E308")}),-1.0]])]});
            var Q14;
            Q14=makeQuery(id+"F0.imprint","IMPRINT",FACE,{"disambiguationData":[TD([[makeQuery(id+"F0.imprint","IMPRINT",EDGE,{"derivedFrom":sQuery(id+"F0.wireOp",EDGE,"E324")}),1.0]])]});
            var Q15;
            Q15=makeQuery(id+"F0.imprint","IMPRINT",FACE,{"disambiguationData":[TD([[makeQuery(id+"F0.imprint","IMPRINT",EDGE,{"derivedFrom":sQuery(id+"F0.wireOp",EDGE,"E372")}),-1.0]])]});
            var Q16;
            Q16=makeQuery(id+"F0.imprint","IMPRINT",FACE,{"disambiguationData":[TD([[makeQuery(id+"F0.imprint","IMPRINT",EDGE,{"derivedFrom":sQuery(id+"F0.wireOp",EDGE,"E425")}),-1.0]])]});
            var Q17;
            Q17=makeQuery(id+"F0.imprint","IMPRINT",FACE,{"disambiguationData":[TD([[makeQuery(id+"F0.imprint","IMPRINT",EDGE,{"derivedFrom":sQuery(id+"F0.wireOp",EDGE,"E478")}),-1.0]])]});
            extrude(context, id + "F2", {"entities" : qUnion([Q0, Q1, Q2, Q3, Q4, Q5, Q6, Q7, Q8, Q9, Q10, Q11, Q12, Q13, Q14, Q15, Q16, Q17]), "oppositeDirection" : true, "depth" : 3.17 * mm});
        }
        {
            var Q0;
            Q0=makeQuery(id+"F2.opExtrude","CAP_FACE",FACE,{"disambiguationData":[OSD([sQuery(id+"F0.wireOp",EDGE,"E504.bottom"),sQuery(id+"F0.wireOp",EDGE,"E504.top"),sQuery(id+"F0.wireOp",EDGE,"E504.left"),sQuery(id+"F0.wireOp",EDGE,"E504.right"),sQuery(id+"F0.wireOp",EDGE,"E505.filletArc"),sQuery(id+"F0.wireOp",EDGE,"E506.filletArc"),sQuery(id+"F0.wireOp",EDGE,"E507.filletArc"),sQuery(id+"F0.wireOp",EDGE,"E508.filletArc"),sQuery(id+"F0.wireOp",EDGE,"E509"),sQuery(id+"F0.wireOp",EDGE,"E510"),sQuery(id+"F0.wireOp",EDGE,"E511"),sQuery(id+"F0.wireOp",EDGE,"E512")])],"isStart":false});
            var sketch = newSketch(context, id + "F3", { "sketchPlane" : qUnion([Q0])});
            skLineSegment(sketch, "E513.0", {"start": v(133.9, 39.63) * mm, "end": v(-133.9, 39.63) * mm});
            skArc(sketch, "E514.0", {"start": v(-146.6, 26.93) * mm, "mid": v(-142.89, 35.9) * mm, "end": v(-133.9, 39.63) * mm});
            skLineSegment(sketch, "E515.0", {"start": v(-146.6, 26.93) * mm, "end": v(-146.6, -26.75) * mm});
            skArc(sketch, "E516.0", {"start": v(-133.9, -39.45) * mm, "mid": v(-142.89, -35.73) * mm, "end": v(-146.6, -26.75) * mm});
            skLineSegment(sketch, "E517.0", {"start": v(133.9, -39.45) * mm, "end": v(-133.9, -39.45) * mm});
            skArc(sketch, "E518.0", {"start": v(146.6, -26.75) * mm, "mid": v(142.89, -35.73) * mm, "end": v(133.9, -39.45) * mm});
            skLineSegment(sketch, "E519.0", {"start": v(146.6, 26.93) * mm, "end": v(146.6, -26.75) * mm});
            skArc(sketch, "E520.0", {"start": v(133.9, 39.63) * mm, "mid": v(142.89, 35.9) * mm, "end": v(146.6, 26.93) * mm});
            skCircle(sketch, "E521.0", {"center": v(-133.9, 26.93) * mm, "radius": 1.59 * mm});
            skCircle(sketch, "E522.0", {"center": v(-133.9, -26.75) * mm, "radius": 1.59 * mm});
            skCircle(sketch, "E523.0", {"center": v(133.9, -26.75) * mm, "radius": 1.59 * mm});
            skCircle(sketch, "E524.0", {"center": v(133.9, 26.93) * mm, "radius": 1.59 * mm});
            skLineSegment(sketch, "E525.1", {"start": v(141.52, 19.3) * mm, "end": v(141.52, -19.13) * mm});
            skLineSegment(sketch, "E525.2", {"start": v(126.28, 34.55) * mm, "end": v(-126.28, 34.55) * mm});
            skLineSegment(sketch, "E525.5", {"start": v(-141.52, 19.3) * mm, "end": v(-141.52, -19.13) * mm});
            skLineSegment(sketch, "E525.7", {"start": v(126.28, -34.37) * mm, "end": v(-126.28, -34.37) * mm});
            skLineSegment(sketch, "E526.top", {"start": v(-141.52, 19.3) * mm, "end": v(-132.63, 19.3) * mm});
            skLineSegment(sketch, "E526.right", {"start": v(-126.28, 34.55) * mm, "end": v(-126.28, 25.66) * mm});
            skLineSegment(sketch, "E527.top", {"start": v(-141.52, -19.13) * mm, "end": v(-132.63, -19.13) * mm});
            skLineSegment(sketch, "E527.right", {"start": v(-126.28, -34.37) * mm, "end": v(-126.28, -25.48) * mm});
            skLineSegment(sketch, "E528.top", {"start": v(141.52, 19.3) * mm, "end": v(132.63, 19.3) * mm});
            skLineSegment(sketch, "E528.right", {"start": v(126.28, 34.55) * mm, "end": v(126.28, 25.66) * mm});
            skLineSegment(sketch, "E529.top", {"start": v(141.52, -19.13) * mm, "end": v(132.63, -19.13) * mm});
            skLineSegment(sketch, "E529.right", {"start": v(126.28, -34.37) * mm, "end": v(126.28, -25.48) * mm});
            skPoint(sketch, "E530.orphan", {"position": v(141.52, 34.55) * mm});
            skPoint(sketch, "E531.orphan", {"position": v(141.52, -34.37) * mm});
            skPoint(sketch, "E532.orphan", {"position": v(-141.52, 34.55) * mm});
            skPoint(sketch, "E533.orphan", {"position": v(-141.52, 26.93) * mm});
            skPoint(sketch, "E534.orphan", {"position": v(-133.9, 34.55) * mm});
            skPoint(sketch, "E535.orphan", {"position": v(-141.52, -34.37) * mm});
            skPoint(sketch, "E536.orphan", {"position": v(-133.9, -34.37) * mm});
            skPoint(sketch, "E527.left.start.orphan", {"position": v(-141.52, -26.75) * mm});
            skPoint(sketch, "E525.0.start.orphan", {"position": v(133.9, 34.55) * mm});
            skPoint(sketch, "E528.left.start.orphan", {"position": v(141.52, 26.93) * mm});
            skPoint(sketch, "E525.3.start.orphan", {"position": v(141.52, -26.75) * mm});
            skPoint(sketch, "E529.bottom.start.orphan", {"position": v(133.9, -34.37) * mm});
            skPoint(sketch, "E537.visualSharp", {"position": v(-126.28, 19.3) * mm});
            skArc(sketch, "E537.filletArc", {"start": v(-132.63, 19.3) * mm, "mid": v(-128.14, 21.17) * mm, "end": v(-126.28, 25.66) * mm});
            skPoint(sketch, "E538.visualSharp", {"position": v(-126.28, -19.13) * mm});
            skArc(sketch, "E538.filletArc", {"start": v(-126.28, -25.48) * mm, "mid": v(-128.14, -20.99) * mm, "end": v(-132.63, -19.13) * mm});
            skPoint(sketch, "E539.visualSharp", {"position": v(126.28, -19.13) * mm});
            skArc(sketch, "E539.filletArc", {"start": v(132.63, -19.13) * mm, "mid": v(128.14, -20.99) * mm, "end": v(126.28, -25.48) * mm});
            skPoint(sketch, "E540.visualSharp", {"position": v(126.28, 19.3) * mm});
            skArc(sketch, "E540.filletArc", {"start": v(126.28, 25.66) * mm, "mid": v(128.14, 21.17) * mm, "end": v(132.63, 19.3) * mm});
            skSolve(sketch);
        }
        {
            var Q0;
            Q0=makeQuery(id+"F3.imprint","IMPRINT",FACE,{"disambiguationData":[TD([[makeQuery(id+"F3.imprint","IMPRINT",EDGE,{"derivedFrom":sQuery(id+"F3.wireOp",EDGE,"E513.0")}),1.0]])]});
            extrude(context, id + "F4", {"entities" : qUnion([Q0]), "depth" : 6.35 * mm});
        }
        {
            var Q0;
            Q0=makeQuery(id+"F4.opExtrude","CAP_FACE",FACE,{"disambiguationData":[OSD([sQuery(id+"F3.wireOp",EDGE,"E513.0"),sQuery(id+"F3.wireOp",EDGE,"E514.0"),sQuery(id+"F3.wireOp",EDGE,"E515.0"),sQuery(id+"F3.wireOp",EDGE,"E516.0"),sQuery(id+"F3.wireOp",EDGE,"E517.0"),sQuery(id+"F3.wireOp",EDGE,"E518.0"),sQuery(id+"F3.wireOp",EDGE,"E519.0"),sQuery(id+"F3.wireOp",EDGE,"E520.0"),sQuery(id+"F3.wireOp",EDGE,"E521.0"),sQuery(id+"F3.wireOp",EDGE,"E522.0"),sQuery(id+"F3.wireOp",EDGE,"E523.0"),sQuery(id+"F3.wireOp",EDGE,"E524.0"),sQuery(id+"F3.wireOp",EDGE,"E525.1"),sQuery(id+"F3.wireOp",EDGE,"E525.2"),sQuery(id+"F3.wireOp",EDGE,"E525.5"),sQuery(id+"F3.wireOp",EDGE,"E525.7"),sQuery(id+"F3.wireOp",EDGE,"E526.top"),sQuery(id+"F3.wireOp",EDGE,"E526.right"),sQuery(id+"F3.wireOp",EDGE,"E527.top"),sQuery(id+"F3.wireOp",EDGE,"E527.right"),sQuery(id+"F3.wireOp",EDGE,"E528.top"),sQuery(id+"F3.wireOp",EDGE,"E528.right"),sQuery(id+"F3.wireOp",EDGE,"E529.top"),sQuery(id+"F3.wireOp",EDGE,"E529.right"),sQuery(id+"F3.wireOp",EDGE,"E537.filletArc"),sQuery(id+"F3.wireOp",EDGE,"E538.filletArc"),sQuery(id+"F3.wireOp",EDGE,"E539.filletArc"),sQuery(id+"F3.wireOp",EDGE,"E540.filletArc")])],"isStart":false});
            var sketch = newSketch(context, id + "F5", { "sketchPlane" : qUnion([Q0])});
            skArc(sketch, "E541.0", {"start": v(-146.6, 26.93) * mm, "mid": v(-142.89, 35.9) * mm, "end": v(-133.9, 39.63) * mm});
            skLineSegment(sketch, "E542.0", {"start": v(133.9, 39.63) * mm, "end": v(-133.9, 39.63) * mm});
            skLineSegment(sketch, "E543.0", {"start": v(-146.6, 26.93) * mm, "end": v(-146.6, -26.75) * mm});
            skArc(sketch, "E544.0", {"start": v(-133.9, -39.45) * mm, "mid": v(-142.89, -35.73) * mm, "end": v(-146.6, -26.75) * mm});
            skArc(sketch, "E545.0", {"start": v(133.9, 39.63) * mm, "mid": v(142.89, 35.9) * mm, "end": v(146.6, 26.93) * mm});
            skLineSegment(sketch, "E546.0", {"start": v(146.6, 26.93) * mm, "end": v(146.6, -26.75) * mm});
            skLineSegment(sketch, "E547.0", {"start": v(133.9, -39.45) * mm, "end": v(-133.9, -39.45) * mm});
            skArc(sketch, "E548.0", {"start": v(146.6, -26.75) * mm, "mid": v(142.89, -35.73) * mm, "end": v(133.9, -39.45) * mm});
            skCircle(sketch, "E549.0", {"center": v(-133.9, 26.93) * mm, "radius": 1.59 * mm});
            skCircle(sketch, "E550.0", {"center": v(-133.9, -26.75) * mm, "radius": 1.59 * mm});
            skCircle(sketch, "E551.0", {"center": v(133.9, -26.75) * mm, "radius": 1.59 * mm});
            skCircle(sketch, "E552.0", {"center": v(133.9, 26.93) * mm, "radius": 1.59 * mm});
            skSolve(sketch);
        }
        {
            var Q0;
            Q0=makeQuery(id+"F5.imprint","IMPRINT",FACE,{"disambiguationData":[TD([[makeQuery(id+"F5.imprint","IMPRINT",EDGE,{"derivedFrom":sQuery(id+"F5.wireOp",EDGE,"E541.0")}),-1.0]])]});
            var Q1;
            Q1=makeQuery(id+"F5.imprint","IMPRINT",FACE,{"disambiguationData":[TD([[makeQuery(id+"F5.imprint","IMPRINT",EDGE,{"derivedFrom":makeQuery(id+"F4.opExtrude","CAP_EDGE",EDGE,{"disambiguationData":[OSD([sQuery(id+"F3.wireOp",EDGE,"E525.1")])],"isStart":false})}),-1.0]])]});
            extrude(context, id + "F6", {"entities" : qUnion([Q0, Q1]), "depth" : 3.17 * mm});
        }
        {
            var Q0;
            Q0=makeQuery(id+"F6.opExtrude","CAP_EDGE",EDGE,{"disambiguationData":[OSD([sQuery(id+"F5.wireOp",EDGE,"E549.0")])],"isStart":false});
            var Q1;
            Q1=makeQuery(id+"F6.opExtrude","CAP_EDGE",EDGE,{"disambiguationData":[OSD([sQuery(id+"F5.wireOp",EDGE,"E550.0")])],"isStart":false});
            var Q2;
            Q2=makeQuery(id+"F6.opExtrude","CAP_EDGE",EDGE,{"disambiguationData":[OSD([sQuery(id+"F5.wireOp",EDGE,"E551.0")])],"isStart":false});
            var Q3;
            Q3=makeQuery(id+"F6.opExtrude","CAP_EDGE",EDGE,{"disambiguationData":[OSD([sQuery(id+"F5.wireOp",EDGE,"E552.0")])],"isStart":false});
            chamfer(context, id + "F7", {"entities" : qUnion([Q0, Q1, Q2, Q3]), "width" : 3.17 * mm, "tangentPropagation" : true});
        }
        {
            var Q0;
            Q0=makeQuery(id+"F6.opExtrude","CAP_FACE",FACE,{"disambiguationData":[OSD([sQuery(id+"F5.wireOp",EDGE,"E541.0"),sQuery(id+"F5.wireOp",EDGE,"E542.0"),sQuery(id+"F5.wireOp",EDGE,"E543.0"),sQuery(id+"F5.wireOp",EDGE,"E544.0"),sQuery(id+"F5.wireOp",EDGE,"E545.0"),sQuery(id+"F5.wireOp",EDGE,"E546.0"),sQuery(id+"F5.wireOp",EDGE,"E547.0"),sQuery(id+"F5.wireOp",EDGE,"E548.0"),sQuery(id+"F5.wireOp",EDGE,"E549.0"),sQuery(id+"F5.wireOp",EDGE,"E550.0"),sQuery(id+"F5.wireOp",EDGE,"E551.0"),sQuery(id+"F5.wireOp",EDGE,"E552.0")])],"isStart":false});
            var sketch = newSketch(context, id + "F8", { "sketchPlane" : qUnion([Q0])});
            skArc(sketch, "E553", {"start": v(-106.92, 14.1) * mm, "mid": v(-108.47, 15.81) * mm, "end": v(-110.1, 14.17) * mm});
            skArc(sketch, "E554", {"start": v(-110.89, 3.63) * mm, "mid": v(-108.5, -1.65) * mm, "end": v(-106.13, 3.63) * mm});
            skLineSegment(sketch, "E555", {"start": v(-110.1, 14.28) * mm, "end": v(-110.1, 5.73) * mm});
            skLineSegment(sketch, "E556", {"start": v(-106.92, 14.35) * mm, "end": v(-106.92, 5.73) * mm});
            skPoint(sketch, "E557.visualSharp", {"position": v(-110.1, 4.28) * mm});
            skArc(sketch, "E557.filletArc", {"start": v(-110.89, 3.63) * mm, "mid": v(-110.3, 4.6) * mm, "end": v(-110.1, 5.73) * mm});
            skPoint(sketch, "E558.visualSharp", {"position": v(-106.92, 4.28) * mm});
            skArc(sketch, "E558.filletArc", {"start": v(-106.92, 5.73) * mm, "mid": v(-106.72, 4.6) * mm, "end": v(-106.13, 3.63) * mm});
            skLineSegment(sketch, "E559", {"start": v(0, 39.63) * mm, "end": v(0, -39.45) * mm, "construction": true});
            skArc(sketch, "E560.MirrorCS", {"start": v(110.89, 3.63) * mm, "mid": v(108.5, -1.65) * mm, "end": v(106.13, 3.63) * mm});
            skArc(sketch, "E561.MirrorCS", {"start": v(110.89, 3.63) * mm, "mid": v(110.3, 4.6) * mm, "end": v(110.1, 5.73) * mm});
            skArc(sketch, "E562.MirrorCS", {"start": v(106.92, 5.73) * mm, "mid": v(106.72, 4.6) * mm, "end": v(106.13, 3.63) * mm});
            skLineSegment(sketch, "E563.MirrorCS", {"start": v(106.92, 14.35) * mm, "end": v(106.92, 5.73) * mm});
            skLineSegment(sketch, "E564.MirrorCS", {"start": v(110.1, 14.28) * mm, "end": v(110.1, 5.73) * mm});
            skArc(sketch, "E565.MirrorCS", {"start": v(106.92, 14.1) * mm, "mid": v(108.47, 15.81) * mm, "end": v(110.1, 14.17) * mm});
            skSolve(sketch);
        }
        {
            var Q0;
            Q0=makeQuery(id+"F8.imprint","IMPRINT",FACE,{"disambiguationData":[TD([[makeQuery(id+"F8.imprint","IMPRINT",EDGE,{"derivedFrom":sQuery(id+"F8.wireOp",EDGE,"E554")}),1.0]])]});
            var Q1;
            Q1=makeQuery(id+"F8.imprint","IMPRINT",FACE,{"disambiguationData":[TD([[makeQuery(id+"F8.imprint","IMPRINT",EDGE,{"derivedFrom":sQuery(id+"F8.wireOp",EDGE,"E560.MirrorCS")}),-1.0]])]});
            extrude(context, id + "F9", {"entities" : qUnion([Q0, Q1]), "operationType" : NewBodyOperationType.REMOVE, "oppositeDirection" : true, "depth" : 6.35 * mm});
        }
    });
